# Revit family: 702-70-103-DN50-600
name_source: partatom
category: Pipe Accessories
units: mm (PartAtom-declared; Revit-internal decimal feet)

## family parameters
Always vertical = Yes
Cut with Voids When Loaded = No
Part Type = Valve - Breaks Into
Round Connector Dimension = Use Diameter
Shared = No
Work Plane-Based = No

## types (14) — shared parameters
DN050_PN10/16 = 702-050-70-134
DN065_PN10/16 = 702-065-70-134
DN080_PN10/16 = 702-080-70-134
DN100_PN10/16 = 702-100-70-134
DN125_PN10/16 = 702-125-70-134
DN150_PN10/16 = 702-150-70-134
DN200_PN10 = 702-200-70-034
DN250_PN10 = 702-250-70-034
DN300_PN10 = 702-300-70-034
DN350_PN10 = 702-350-70-034
DN400_PN10 = 702-400-70-034
DN450_PN10 = 702-450-70-034
DN500_PN10 = 702-500-70-034
DN600_PN10 = 702-600-70-034
Description_ = AVK KNIFE GATE VALVE
Search_table = 702-70-103-DN50-600
URL product pages = https://www.avkvalves.com

## per-type parameters (varying)
- DN 050: B2_Ref=79 mm; Body_width=87 mm; Bonnet_height=273 mm; Bonnet_height_2=150 mm; D=514 mm; Flange_Thickness=5 mm  [stored 0.0164042 ft]; H=300 mm; H1=588 mm; H1_Ref_2=90 mm; H3=653 mm; H4=160 mm; H4_off=120 mm; H4_off_ref=70 mm  [stored 0.229659 ft]; HW_Dia=10 mm  [stored 0.0328084 ft]; H_Ref=114 mm; Ho=407 mm; ID=25 mm  [stored 0.082021 ft]; L=43 mm  [stored 0.141076 ft]; L2=47 mm  [stored 0.154199 ft]; Name_Ref=170 mm; Neck_Rod=10 mm  [stored 0.0328084 ft]; Nominal Diameter (DN)=50 mm  [stored 0.164042 ft]; Top_flange=63 mm; Top_flange2=288 mm; W=131 mm; W2=66 mm  [stored 0.216535 ft]; W3=55 mm  [stored 0.180446 ft]; W3_ref=150 mm; W4=36 mm; W5=30 mm  [stored 0.0984252 ft]; W6=20 mm  [stored 0.0656168 ft]
- DN 065: B2_Ref=86 mm; Body_width=95 mm; Bonnet_height=295 mm; Bonnet_height_2=163 mm; D=514 mm; Flange_Thickness=5 mm  [stored 0.0164042 ft]; H=325 mm; H1=613 mm; H1_Ref_2=90 mm; H3=685 mm; H4=160 mm; H4_off=120 mm; H4_off_ref=70 mm  [stored 0.229659 ft]; HW_Dia=10 mm  [stored 0.0328084 ft]; H_Ref=124 mm; Ho=444 mm; ID=33 mm; L=46 mm  [stored 0.150919 ft]; L2=51 mm  [stored 0.167323 ft]; Name_Ref=186 mm; Neck_Rod=10 mm  [stored 0.0328084 ft]; Nominal Diameter (DN)=65 mm  [stored 0.213255 ft]; Top_flange=63 mm; Top_flange2=288 mm; W=143 mm; W2=72 mm; W3=60 mm  [stored 0.19685 ft]; W3_ref=150 mm; W4=40 mm  [stored 0.131234 ft]; W5=33 mm; W6=22 mm
- DN 080: B2_Ref=110 mm; Body_width=123 mm; Bonnet_height=325 mm; Bonnet_height_2=179 mm; D=514 mm; Flange_Thickness=5 mm  [stored 0.0164042 ft]; H=357 mm; H1=645 mm; H1_Ref_2=100 mm; H3=737 mm; H4=160 mm; H4_off=120 mm; H4_off_ref=70 mm  [stored 0.229659 ft]; HW_Dia=15 mm  [stored 0.0492126 ft]; H_Ref=159 mm; Ho=499 mm; ID=40 mm  [stored 0.131234 ft]; L=46 mm  [stored 0.150919 ft]; L2=51 mm  [stored 0.167323 ft]; Name_Ref=239 mm; Neck_Rod=10 mm  [stored 0.0328084 ft]; Nominal Diameter (DN)=80 mm  [stored 0.262467 ft]; Top_flange=63 mm; Top_flange2=288 mm; W=184 mm; W2=92 mm; W3=77 mm; W3_ref=160 mm; W4=51 mm  [stored 0.167323 ft]; W5=43 mm  [stored 0.141076 ft]; W6=28 mm
- DN 100: B2_Ref=121 mm; Body_width=135 mm; Bonnet_height=356 mm; Bonnet_height_2=196 mm; D=514 mm; Flange_Thickness=5 mm  [stored 0.0164042 ft]; H=392 mm; H1=680 mm; H1_Ref_2=110 mm; H3=781 mm; H4=160 mm; H4_off=120 mm; H4_off_ref=70 mm  [stored 0.229659 ft]; HW_Dia=15 mm  [stored 0.0492126 ft]; H_Ref=175 mm; Ho=582 mm; ID=50 mm  [stored 0.164042 ft]; L=52 mm  [stored 0.170604 ft]; L2=57 mm; Name_Ref=263 mm; Neck_Rod=10 mm  [stored 0.0328084 ft]; Nominal Diameter (DN)=100 mm; Top_flange=63 mm; Top_flange2=288 mm; W=202 mm; W2=101 mm; W3=84 mm; W3_ref=170 mm; W4=56 mm  [stored 0.183727 ft]; W5=47 mm  [stored 0.154199 ft]; W6=31 mm
- DN 125: B2_Ref=138 mm; Body_width=153 mm; Bonnet_height=389 mm; Bonnet_height_2=214 mm; D=514 mm; Flange_Thickness=5 mm  [stored 0.0164042 ft]; H=428 mm; H1=716 mm; H1_Ref_2=148 mm; H3=831 mm; H4=160 mm; H4_off=120 mm; H4_off_ref=70 mm  [stored 0.229659 ft]; HW_Dia=25 mm  [stored 0.082021 ft]; H_Ref=199 mm; Ho=618 mm; ID=63 mm; L=56 mm  [stored 0.183727 ft]; L2=62 mm; Name_Ref=299 mm; Neck_Rod=10 mm  [stored 0.0328084 ft]; Nominal Diameter (DN)=125 mm; Top_flange=63 mm; Top_flange2=288 mm; W=230 mm; W2=115 mm; W3=96 mm; W3_ref=240 mm; W4=64 mm; W5=53 mm; W6=35 mm  [stored 0.114829 ft]
- DN 150: B2_Ref=162 mm; Body_width=180 mm; Bonnet_height=464 mm; Bonnet_height_2=255 mm; D=514 mm; Flange_Thickness=5 mm  [stored 0.0164042 ft]; H=510 mm; H1=798 mm; H1_Ref_2=148 mm; H3=933 mm; H4=160 mm; H4_off=120 mm; H4_off_ref=70 mm  [stored 0.229659 ft]; HW_Dia=25 mm  [stored 0.082021 ft]; H_Ref=234 mm; Ho=732 mm; ID=75 mm; L=56 mm  [stored 0.183727 ft]; L2=62 mm; Name_Ref=351 mm; Neck_Rod=10 mm  [stored 0.0328084 ft]; Nominal Diameter (DN)=150 mm; Top_flange=63 mm; Top_flange2=288 mm; W=270 mm; W2=135 mm; W3=113 mm; W3_ref=240 mm; W4=75 mm; W5=63 mm; W6=42 mm
- DN 200: B2_Ref=199 mm; Body_width=221 mm; Bonnet_height=555 mm; Bonnet_height_2=305 mm; D=514 mm; Flange_Thickness=10 mm  [stored 0.0328084 ft]; H=610 mm; H1=898 mm; H1_Ref_2=158 mm; H3=1063 mm; H4=200 mm; H4_off=160 mm; H4_off_ref=90 mm; HW_Dia=25 mm  [stored 0.082021 ft]; H_Ref=287 mm; Ho=882 mm; ID=100 mm; L=60 mm  [stored 0.19685 ft]; L2=66 mm  [stored 0.216535 ft]; Name_Ref=430 mm; Neck_Rod=20 mm  [stored 0.0656168 ft]; Nominal Diameter (DN)=200 mm; Top_flange=63 mm; Top_flange2=288 mm; W=331 mm; W2=166 mm; W3=138 mm; W3_ref=240 mm; W4=92 mm; W5=77 mm; W6=51 mm  [stored 0.167323 ft]
- DN 250: B2_Ref=238 mm; Body_width=265 mm; Bonnet_height=651 mm; Bonnet_height_2=358 mm; D=537 mm; Flange_Thickness=10 mm  [stored 0.0328084 ft]; H=716 mm; H1=1006 mm; H1_Ref_2=165 mm; H3=1204 mm; H4=315 mm; H4_off=275 mm; H4_off_ref=148 mm; HW_Dia=30 mm  [stored 0.0984252 ft]; H_Ref=344 mm; Ho=1044 mm; ID=125 mm; L=68 mm  [stored 0.223097 ft]; L2=75 mm; Name_Ref=516 mm; Neck_Rod=20 mm  [stored 0.0656168 ft]; Nominal Diameter (DN)=250 mm; Top_flange=88 mm; Top_flange2=290 mm; W=397 mm; W2=199 mm; W3=165 mm; W3_ref=240 mm; W4=110 mm; W5=92 mm; W6=61 mm
- DN 300: B2_Ref=271 mm; Body_width=301 mm; Bonnet_height=758 mm; Bonnet_height_2=417 mm; D=537 mm; Flange_Thickness=15 mm  [stored 0.0492126 ft]; H=834 mm; H1=1124 mm; H1_Ref_2=190 mm; H3=1350 mm; H4=315 mm; H4_off=275 mm; H4_off_ref=148 mm; HW_Dia=30 mm  [stored 0.0984252 ft]; H_Ref=392 mm; Ho=1219 mm; ID=150 mm; L=78 mm  [stored 0.255906 ft]; L2=86 mm; Name_Ref=588 mm; Neck_Rod=30 mm  [stored 0.0984252 ft]; Nominal Diameter (DN)=300 mm; Top_flange=88 mm; Top_flange2=290 mm; W=452 mm; W2=226 mm; W3=188 mm; W3_ref=285 mm; W4=126 mm; W5=105 mm; W6=70 mm  [stored 0.229659 ft]
- DN 350: B2_Ref=311 mm; Body_width=345 mm; Bonnet_height=843 mm; Bonnet_height_2=464 mm; D=537 mm; Flange_Thickness=15 mm  [stored 0.0492126 ft]; H=927 mm; H1=1217 mm; H1_Ref_2=191 mm; H3=1476 mm; H4=400 mm; H4_off=360 mm; H4_off_ref=190 mm; HW_Dia=30 mm  [stored 0.0984252 ft]; H_Ref=449 mm; Ho=1362 mm; ID=175 mm; L=78 mm  [stored 0.255906 ft]; L2=86 mm; Name_Ref=673 mm; Neck_Rod=30 mm  [stored 0.0984252 ft]; Nominal Diameter (DN)=350 mm; Top_flange=110 mm; Top_flange2=290 mm; W=518 mm; W2=259 mm; W3=216 mm; W3_ref=285 mm; W4=144 mm; W5=120 mm; W6=80 mm  [stored 0.262467 ft]
- DN 400: B2_Ref=346 mm; Body_width=384 mm; Bonnet_height=941 mm; Bonnet_height_2=518 mm; D=537 mm; Flange_Thickness=20 mm  [stored 0.0656168 ft]; H=1035 mm; H1=1325 mm; H1_Ref_2=205 mm; H3=1613 mm; H4=400 mm; H4_off=360 mm; H4_off_ref=190 mm; HW_Dia=35 mm  [stored 0.114829 ft]; H_Ref=499 mm; Ho=1510 mm; ID=200 mm; L=90 mm; L2=99 mm; Name_Ref=749 mm; Neck_Rod=40 mm  [stored 0.131234 ft]; Nominal Diameter (DN)=400 mm; Top_flange=110 mm; Top_flange2=290 mm; W=576 mm; W2=288 mm; W3=240 mm; W3_ref=300 mm; W4=160 mm; W5=133 mm; W6=89 mm
- DN 450: B2_Ref=371 mm; Body_width=412 mm; Bonnet_height=1061 mm; Bonnet_height_2=584 mm; D=728 mm; Flange_Thickness=20 mm  [stored 0.0656168 ft]; H=1167 mm; H1=1566 mm; H1_Ref_2=220 mm; H3=1879 mm; H4=450 mm; H4_off=410 mm; H4_off_ref=215 mm; HW_Dia=35 mm  [stored 0.114829 ft]; H_Ref=536 mm; Ho=1717 mm; ID=225 mm; L=90 mm; L2=99 mm; Name_Ref=803 mm; Neck_Rod=40 mm  [stored 0.131234 ft]; Nominal Diameter (DN)=450 mm; Top_flange=120 mm; Top_flange2=399 mm; W=618 mm; W2=309 mm; W3=258 mm; W3_ref=320 mm; W4=172 mm; W5=143 mm; W6=95 mm
- DN 500: B2_Ref=419 mm; Body_width=465 mm; Bonnet_height=1101 mm; Bonnet_height_2=606 mm; D=728 mm; Flange_Thickness=20 mm  [stored 0.0656168 ft]; H=1211 mm; H1=1610 mm; H1_Ref_2=245 mm; H3=1959 mm; H4=450 mm; H4_off=410 mm; H4_off_ref=215 mm; HW_Dia=35 mm  [stored 0.114829 ft]; H_Ref=605 mm; Ho=1826 mm; ID=250 mm; L=95 mm; L2=105 mm; Name_Ref=907 mm; Neck_Rod=40 mm  [stored 0.131234 ft]; Nominal Diameter (DN)=500 mm; Top_flange=120 mm; Top_flange2=399 mm; W=698 mm; W2=349 mm; W3=291 mm; W3_ref=350 mm; W4=194 mm; W5=162 mm; W6=108 mm
- DN 600: B2_Ref=490 mm; Body_width=545 mm; Bonnet_height=1273 mm; Bonnet_height_2=700 mm; D=728 mm; Flange_Thickness=20 mm  [stored 0.0656168 ft]; H=1400 mm; H1=1799 mm; H1_Ref_2=285 mm; H3=2207 mm; H4=450 mm; H4_off=410 mm; H4_off_ref=215 mm; HW_Dia=35 mm  [stored 0.114829 ft]; H_Ref=708 mm; Ho=2115 mm; ID=300 mm; L=105 mm; L2=116 mm; Name_Ref=1062 mm; Neck_Rod=40 mm  [stored 0.131234 ft]; Nominal Diameter (DN)=600 mm; Top_flange=120 mm; Top_flange2=399 mm; W=817 mm; W2=409 mm; W3=340 mm; W3_ref=410 mm; W4=227 mm; W5=189 mm; W6=126 mm

note: [stored X ft] marks values corroborated as IEEE doubles in the binary element streams (Revit-internal decimal feet)

## geometry (parser evidence)
native form markers: Sweep x6
no freeform markers — native parametric forms only
